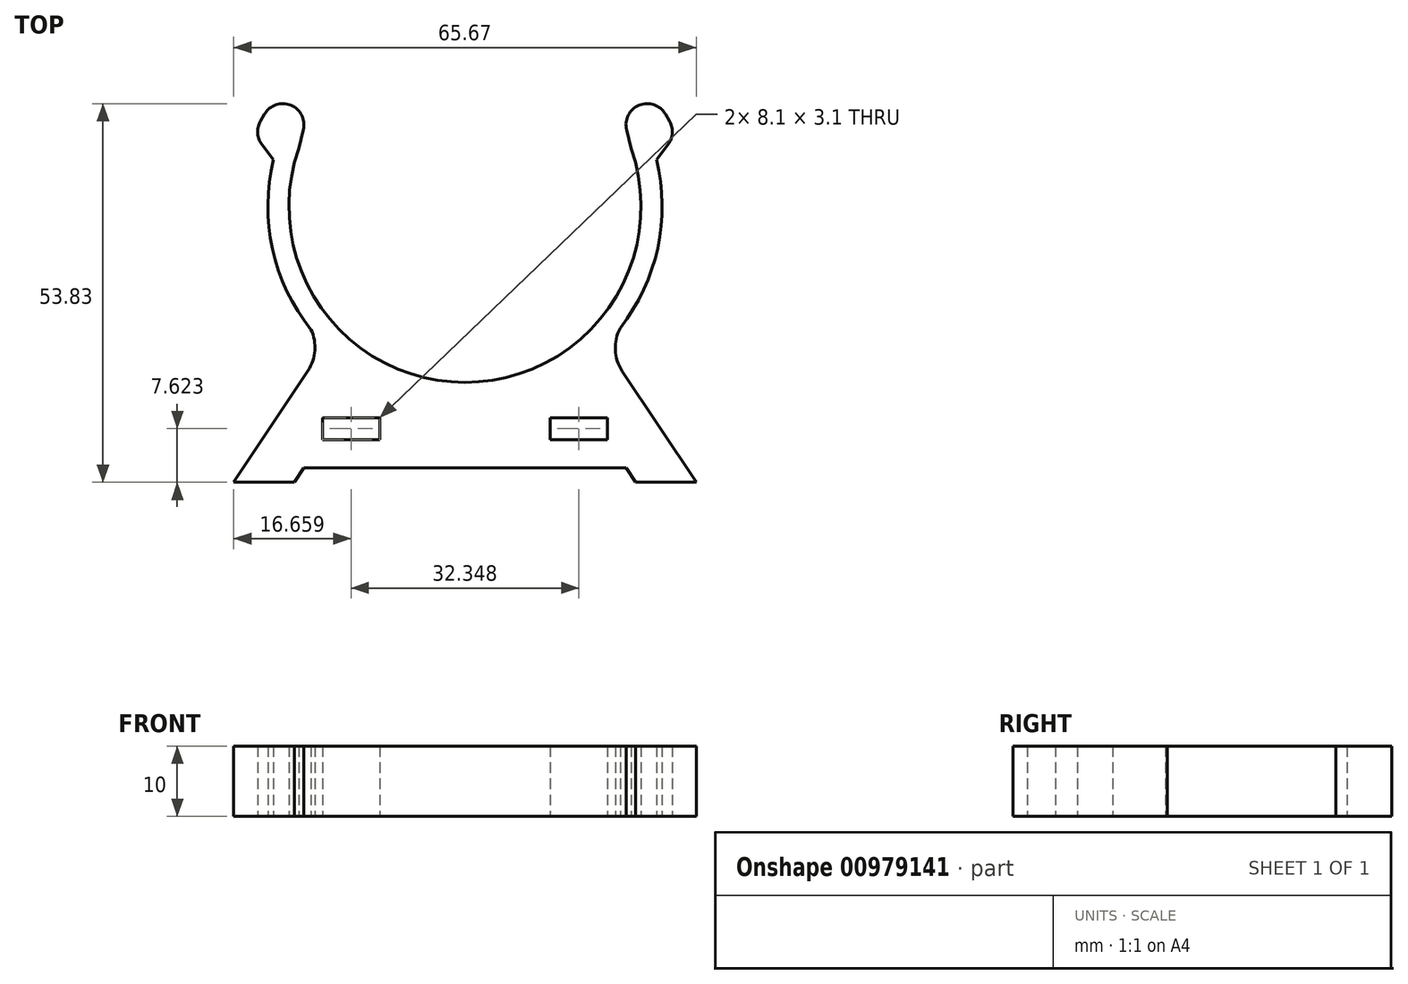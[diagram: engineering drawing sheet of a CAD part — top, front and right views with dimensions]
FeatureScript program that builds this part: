
annotation { "Feature Type Name" : "Feature", "Feature Type Description" : "" }
export const myFeature = defineFeature(function(context is Context, id is Id, definition is map)
    precondition{}
    {
        {
            var Q0;
            Q0=qCreatedBy(makeId("Top.planeOp"),FACE);
            var sketch = newSketch(context, id + "F0", { "sketchPlane" : qUnion([Q0])});
            skPoint(sketch, "E0.middle", {"position": v(0, 22.9) * mm});
            skLineSegment(sketch, "E1", {"start": v(-24.16, -0.44) * mm, "end": v(-34.7, -16.3) * mm});
            skLineSegment(sketch, "E2", {"start": v(-34.7, -16.3) * mm, "end": v(-26.1, -16.3) * mm});
            skLineSegment(sketch, "E3", {"start": v(-26.1, -16.3) * mm, "end": v(-24.73, -14.23) * mm});
            skLineSegment(sketch, "E4", {"start": v(-24.73, -14.23) * mm, "end": v(-1.86, -14.23) * mm});
            skLineSegment(sketch, "E5.MirrorCS", {"start": v(22.39, -16.3) * mm, "end": v(21.01, -14.23) * mm});
            skLineSegment(sketch, "E6.MirrorCS", {"start": v(21.01, -14.23) * mm, "end": v(-1.86, -14.23) * mm});
            skLineSegment(sketch, "E7.MirrorCS", {"start": v(30.98, -16.3) * mm, "end": v(22.39, -16.3) * mm});
            skLineSegment(sketch, "E8.MirrorCS", {"start": v(20.48, -0.5) * mm, "end": v(30.98, -16.3) * mm});
            skLineSegment(sketch, "E9.bottom", {"start": v(-22.08, -7.13) * mm, "end": v(-13.98, -7.13) * mm});
            skLineSegment(sketch, "E9.top", {"start": v(-22.08, -10.23) * mm, "end": v(-13.98, -10.23) * mm});
            skLineSegment(sketch, "E9.left", {"start": v(-22.08, -7.13) * mm, "end": v(-22.08, -10.23) * mm});
            skLineSegment(sketch, "E9.right", {"start": v(-13.98, -7.13) * mm, "end": v(-13.98, -10.23) * mm});
            skLineSegment(sketch, "E10.MirrorCS", {"start": v(18.37, -7.13) * mm, "end": v(18.37, -10.23) * mm});
            skLineSegment(sketch, "E11.MirrorCS", {"start": v(18.37, -10.23) * mm, "end": v(10.27, -10.23) * mm});
            skLineSegment(sketch, "E12.MirrorCS", {"start": v(18.37, -7.13) * mm, "end": v(10.27, -7.13) * mm});
            skLineSegment(sketch, "E13.MirrorCS", {"start": v(10.27, -7.13) * mm, "end": v(10.27, -10.23) * mm});
            skPoint(sketch, "E14.visualSharp", {"position": v(-24.96, -1.64) * mm});
            skArc(sketch, "E14.filletArc", {"start": v(-24.16, -0.44) * mm, "mid": v(-23.17, 2.42) * mm, "end": v(-23.71, 5.4) * mm});
            skPoint(sketch, "E15.visualSharp", {"position": v(21.24, -1.64) * mm});
            skArc(sketch, "E15.filletArc", {"start": v(20.2, 5.65) * mm, "mid": v(19.49, 2.53) * mm, "end": v(20.48, -0.5) * mm});
            skPoint(sketch, "E16.visualSharp", {"position": v(-21.96, 4.81) * mm});
            skPoint(sketch, "E17.visualSharp", {"position": v(18.4, 4.81) * mm});
            skPoint(sketch, "E18.newPointA", {"position": v(31.83, 23.8) * mm});
            skLineSegment(sketch, "E19", {"start": v(21.24, 23.8) * mm, "end": v(21.4, 23.8) * mm});
            skLineSegment(sketch, "E20", {"start": v(-26.1, -16.3) * mm, "end": v(22.39, -16.3) * mm, "construction": true});
            skLineSegment(sketch, "E21", {"start": v(-1.86, -4.8) * mm, "end": v(-1.86, 37.92) * mm, "construction": true});
            skLineSegment(sketch, "E22", {"start": v(0, 22.9) * mm, "end": v(-11.1, 22.9) * mm, "construction": true});
            skCircle(sketch, "E23", {"center": v(-1.86, 22.9) * mm, "radius": 25 * mm});
            skCircle(sketch, "E24", {"center": v(-1.86, 22.9) * mm, "radius": 28 * mm});
            skLineSegment(sketch, "E25", {"start": v(-25.46, 31.14) * mm, "end": v(-24.8, 33.81) * mm});
            skLineSegment(sketch, "E26", {"start": v(-30.31, 36.03) * mm, "end": v(-30.91, 35) * mm});
            skLineSegment(sketch, "E27", {"start": v(-30.68, 31.65) * mm, "end": v(-29.05, 29.57) * mm});
            skPoint(sketch, "E28.visualSharp", {"position": v(-31.93, 33.25) * mm});
            skArc(sketch, "E28.filletArc", {"start": v(-30.91, 35) * mm, "mid": v(-31.3, 33.3) * mm, "end": v(-30.68, 31.65) * mm});
            skPoint(sketch, "E29.visualSharp", {"position": v(-19.8, 54.2) * mm});
            skArc(sketch, "E29.filletArc", {"start": v(-24.8, 33.81) * mm, "mid": v(-26.6, 37.31) * mm, "end": v(-30.31, 36.03) * mm});
            skLineSegment(sketch, "E30.MirrorCS", {"start": v(26.6, 36.03) * mm, "end": v(27.2, 35) * mm});
            skLineSegment(sketch, "E31.MirrorCS", {"start": v(26.96, 31.65) * mm, "end": v(25.34, 29.57) * mm});
            skLineSegment(sketch, "E32.MirrorCS", {"start": v(21.75, 31.14) * mm, "end": v(21.1, 33.81) * mm});
            skArc(sketch, "E33.MirrorCS", {"start": v(27.2, 35) * mm, "mid": v(27.6, 33.3) * mm, "end": v(26.96, 31.65) * mm});
            skPoint(sketch, "E34.MirrorP", {"position": v(28.21, 33.25) * mm});
            skArc(sketch, "E35.MirrorCS", {"start": v(21.1, 33.81) * mm, "mid": v(22.88, 37.31) * mm, "end": v(26.6, 36.03) * mm});
            skSolve(sketch);
        }
        {
            var Q0;
            {var subQ9=sQuery(id+"F0.wireOp",EDGE,"E25");Q0=makeQuery(id+"F0.imprint","IMPRINT",FACE,{"disambiguationData":[TD([[makeQuery(id+"F0.imprint","IMPRINT",EDGE,{"derivedFrom":subQ9}),1.0]])]});}
            var Q1;
            {var subQ1=sQuery(id+"F0.wireOp",EDGE,"E26");Q1=makeQuery(id+"F0.imprint","IMPRINT",FACE,{"disambiguationData":[TD([[makeQuery(id+"F0.imprint","IMPRINT",EDGE,{"derivedFrom":subQ1}),1.0]])]});}
            var Q2;
            {var subQ1=sQuery(id+"F0.wireOp",EDGE,"E30.MirrorCS");Q2=makeQuery(id+"F0.imprint","IMPRINT",FACE,{"disambiguationData":[TD([[makeQuery(id+"F0.imprint","IMPRINT",EDGE,{"derivedFrom":subQ1}),-1.0]])]});}
            var Q3;
            Q3=makeQuery(id+"F0.imprint","IMPRINT",FACE,{"disambiguationData":[TD([[makeQuery(id+"F0.imprint","IMPRINT",EDGE,{"derivedFrom":sQuery(id+"F0.wireOp",EDGE,"E1")}),1.0]])]});
            extrude(context, id + "F1", {"entities" : qUnion([Q0, Q1, Q2, Q3]), "depth" : 10 * mm, "offsetDistance" : 25 * mm});
        }
    });
